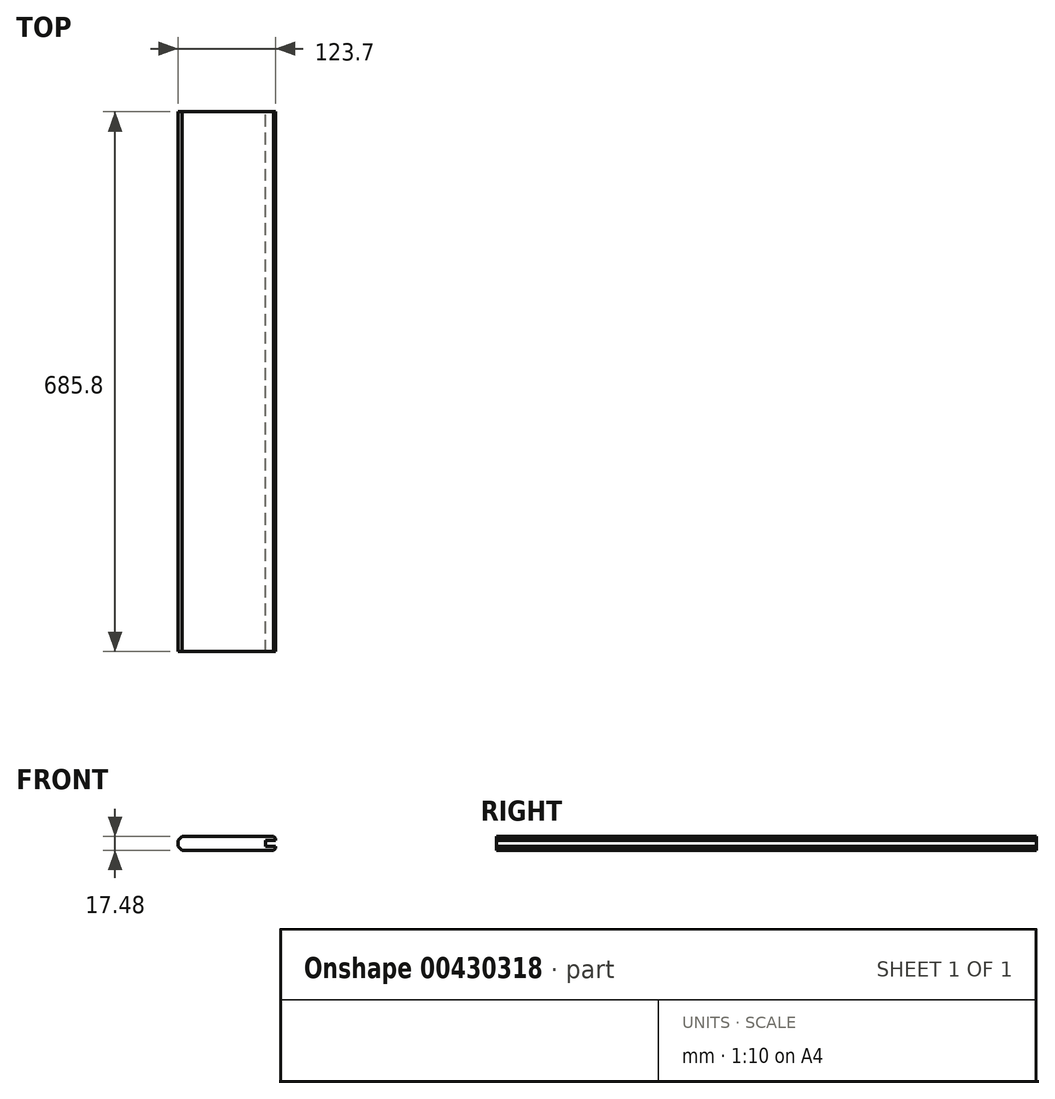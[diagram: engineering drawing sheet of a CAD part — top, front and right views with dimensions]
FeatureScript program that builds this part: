
annotation { "Feature Type Name" : "Feature", "Feature Type Description" : "" }
export const myFeature = defineFeature(function(context is Context, id is Id, definition is map)
    precondition{}
    {
        {
            var Q0;
            Q0=qCreatedBy(makeId("Front.planeOp"),FACE);
            var sketch = newSketch(context, id + "F0", { "sketchPlane" : qUnion([Q0])});
            skLineSegment(sketch, "E0.bottom", {"start": v(68.2, 8.74) * mm, "end": v(-55.5, 8.74) * mm});
            skLineSegment(sketch, "E0.top", {"start": v(68.2, -8.74) * mm, "end": v(-55.5, -8.74) * mm});
            skLineSegment(sketch, "E0.left", {"start": v(68.2, 8.74) * mm, "end": v(68.2, 3.66) * mm});
            skLineSegment(sketch, "E0.right", {"start": v(-68.2, 3.66) * mm, "end": v(-68.2, -3.66) * mm});
            skPoint(sketch, "E0.middle", {"position": v(0, 0) * mm});
            skLineSegment(sketch, "E1.bottom", {"start": v(68.2, 3.66) * mm, "end": v(55.5, 3.66) * mm});
            skLineSegment(sketch, "E1.top", {"start": v(68.2, -3.66) * mm, "end": v(55.5, -3.66) * mm});
            skLineSegment(sketch, "E1.right", {"start": v(55.5, 3.66) * mm, "end": v(55.5, -3.66) * mm});
            skPoint(sketch, "E1.middle", {"position": v(68.2, 0) * mm});
            skPoint(sketch, "E1.left.end.orphan", {"position": v(80.9, -3.66) * mm});
            skPoint(sketch, "E1.left.start.orphan", {"position": v(80.9, 3.66) * mm});
            skLineSegment(sketch, "E2.trimOffspring", {"start": v(68.2, -3.66) * mm, "end": v(68.2, -8.74) * mm});
            skLineSegment(sketch, "E3.bottom", {"start": v(-68.2, 3.66) * mm, "end": v(-55.5, 3.66) * mm});
            skLineSegment(sketch, "E3.right", {"start": v(-55.5, 3.66) * mm, "end": v(-55.5, 8.74) * mm});
            skLineSegment(sketch, "E4.top", {"start": v(-68.2, -3.66) * mm, "end": v(-55.5, -3.66) * mm});
            skLineSegment(sketch, "E4.right", {"start": v(-55.5, -8.74) * mm, "end": v(-55.5, -3.66) * mm});
            skPoint(sketch, "E5.orphan", {"position": v(-68.2, 8.74) * mm});
            skPoint(sketch, "E6.orphan", {"position": v(-68.2, -8.74) * mm});
            skSolve(sketch);
        }
        {
            var Q0;
            Q0=makeQuery(id+"F0.imprint","IMPRINT",FACE,{"disambiguationData":[TD([[makeQuery(id+"F0.imprint","IMPRINT",EDGE,{"derivedFrom":sQuery(id+"F0.wireOp",EDGE,"E0.bottom")}),1.0]])]});
            extrude(context, id + "F1", {"entities" : qUnion([Q0]), "depth" : 685.8 * mm});
        }
        {
            var Q0;
            Q0=makeQuery(id+"F1.opExtrude","SWEPT_EDGE",EDGE,{"disambiguationData":[OSD([sQuery(id+"F0.wireOp",EDGE,"E0.bottom"),sQuery(id+"F0.wireOp",EDGE,"E0.left")])]});
            var Q1;
            Q1=makeQuery(id+"F1.opExtrude","SWEPT_EDGE",EDGE,{"disambiguationData":[OSD([sQuery(id+"F0.wireOp",EDGE,"E0.top"),sQuery(id+"F0.wireOp",EDGE,"E2.trimOffspring")])]});
            var Q2;
            Q2=makeQuery(id+"F1.opExtrude","SWEPT_EDGE",EDGE,{"disambiguationData":[OSD([sQuery(id+"F0.wireOp",EDGE,"E0.right"),sQuery(id+"F0.wireOp",EDGE,"E3.bottom")])]});
            var Q3;
            Q3=makeQuery(id+"F1.opExtrude","SWEPT_EDGE",EDGE,{"disambiguationData":[OSD([sQuery(id+"F0.wireOp",EDGE,"E0.right"),sQuery(id+"F0.wireOp",EDGE,"E4.top")])]});
            chamfer(context, id + "F2", {"entities" : qUnion([Q0, Q1, Q2, Q3]), "width" : 2.54 * mm, "tangentPropagation" : true});
        }
        {
            var Q0;
            Q0=makeQuery(id+"F1.opExtrude","SWEPT_EDGE",EDGE,{"disambiguationData":[OSD([sQuery(id+"F0.wireOp",EDGE,"E0.bottom"),sQuery(id+"F0.wireOp",EDGE,"E3.right")])]});
            var Q1;
            Q1=makeQuery(id+"F1.opExtrude","SWEPT_EDGE",EDGE,{"disambiguationData":[OSD([sQuery(id+"F0.wireOp",EDGE,"E0.top"),sQuery(id+"F0.wireOp",EDGE,"E4.right")])]});
            chamfer(context, id + "F3", {"entities" : qUnion([Q0, Q1]), "width" : 5.08 * mm, "tangentPropagation" : true});
        }
        {
            var Q0;
            Q0=makeQuery(id+"F1.opExtrude","CAP_FACE",FACE,{"disambiguationData":[OSD([sQuery(id+"F0.wireOp",EDGE,"E0.bottom"),sQuery(id+"F0.wireOp",EDGE,"E0.top"),sQuery(id+"F0.wireOp",EDGE,"E0.left"),sQuery(id+"F0.wireOp",EDGE,"E0.right"),sQuery(id+"F0.wireOp",EDGE,"E1.bottom"),sQuery(id+"F0.wireOp",EDGE,"E1.top"),sQuery(id+"F0.wireOp",EDGE,"E1.right"),sQuery(id+"F0.wireOp",EDGE,"E2.trimOffspring"),sQuery(id+"F0.wireOp",EDGE,"E3.bottom"),sQuery(id+"F0.wireOp",EDGE,"E3.right"),sQuery(id+"F0.wireOp",EDGE,"E4.top"),sQuery(id+"F0.wireOp",EDGE,"E4.right")])],"isStart":false});
            var sketch = newSketch(context, id + "F4", { "sketchPlane" : qUnion([Q0])});
            skLineSegment(sketch, "E7.bottom", {"start": v(-55.5, 3.66) * mm, "end": v(-80.9, 3.66) * mm});
            skLineSegment(sketch, "E7.top", {"start": v(-55.5, -3.66) * mm, "end": v(-80.9, -3.66) * mm});
            skLineSegment(sketch, "E7.left", {"start": v(-55.5, 3.66) * mm, "end": v(-55.5, -3.66) * mm});
            skLineSegment(sketch, "E7.right", {"start": v(-80.9, 3.66) * mm, "end": v(-80.9, -3.66) * mm});
            skPoint(sketch, "E7.middle", {"position": v(-68.2, 0) * mm});
            skSolve(sketch);
        }
        {
            var Q0;
            Q0 = qSketchRegion(id + "F4", true);
            extrude(context, id + "F5", {"entities" : qUnion([Q0]), "operationType" : NewBodyOperationType.REMOVE, "endBound" : BoundingType.THROUGH_ALL, "oppositeDirection" : true, "depth" : 25.4 * mm});
        }
    });
